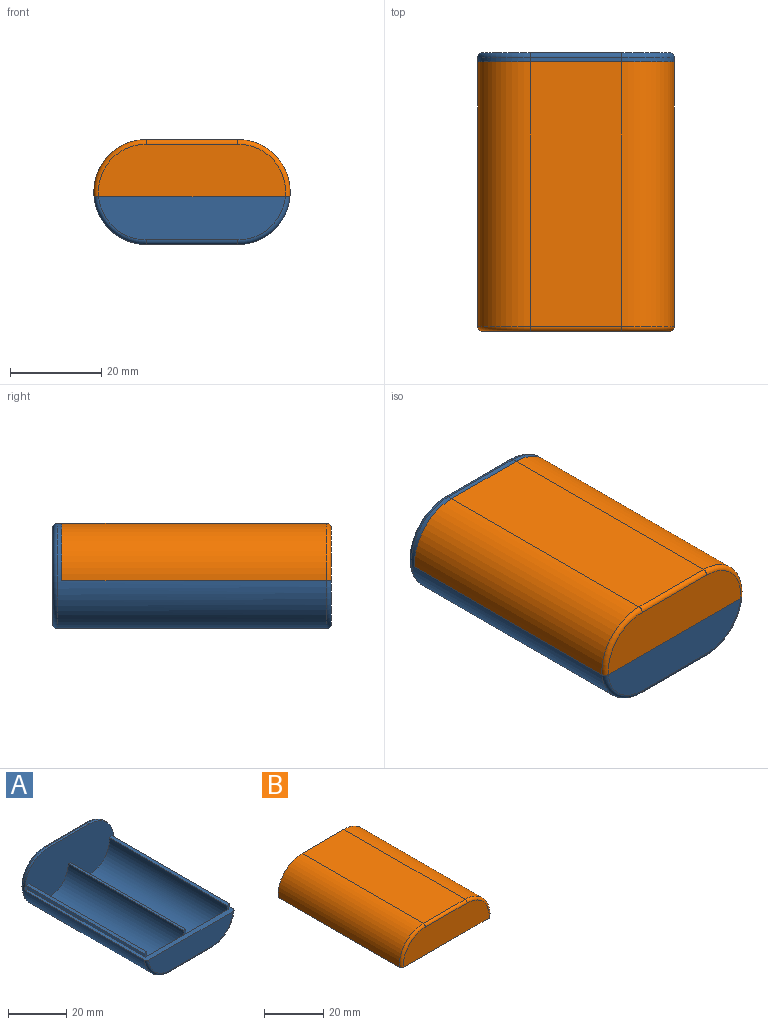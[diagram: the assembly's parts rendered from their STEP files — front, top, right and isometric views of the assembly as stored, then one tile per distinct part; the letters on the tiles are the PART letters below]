
ASSEMBLY  parts=2 mates=1
PART A: 27 faces, bbox 44.9x61x24.9 mm
  f0: plane 2x1.42mm, normal (0,-1,0), area 2mm2, adj f10,f11,f12,f13
  f1: plane 2x1.42mm, normal (0,-1,0), area 2mm2, adj f7,f8,f9,f10
  f2: cylinder r=11.5mm len=59mm, axis (0,-1,0), area 1025.8mm2, adj f3,f5,f10,f15,f20,f25
  f3: plane 20x1mm, normal (0,0,1), area 20mm2, adj f2,f4,f15,f21
  f4: cylinder r=11.5mm len=59mm, axis (0,-1,0), area 1025.8mm2, adj f3,f5,f10,f15,f23,f24
  f5: plane 59x20mm, normal (0,0,-1), area 1180mm2, adj f2,f4,f22,f26
  f6: plane 41x21mm, normal (0,1,0), area 766.4mm2, adj f20,f21,f22,f23
  f7: cylinder r=9.5mm len=57mm, axis (0,-1,0), area 1743.4mm2, adj f1,f8,f14,f15,f16,f18,f19
  f8: plane 57x1.42mm, normal (0,0,1), area 80.8mm2, adj f1,f7,f9,f15
  f9: plane 57x2mm, normal (0.94,0,-0.34), area 121.3mm2, adj f1,f8,f10,f15
  f10: plane 59x42.91mm, normal (0,0,1), area 235.9mm2, adj f0,f1,f2,f4,f9,f11,f15,f16
  f11: plane 57x2mm, normal (-0.94,0,-0.34), area 121.3mm2, adj f0,f10,f12,f15
  f12: plane 57x1.42mm, normal (0,0,1), area 80.8mm2, adj f0,f11,f13,f15
  f13: cylinder r=9.5mm len=57mm, axis (0,-1,0), area 1743.4mm2, adj f0,f12,f14,f15,f16,f18,f19
  f14: plane 56x1mm, normal (0,0,1), area 56mm2, adj f7,f13,f15,f19
  f15: plane 43x21mm, normal (0,-1,0), area 721.2mm2, adj f2,f3,f4,f7,f8,f9,f10,f11
  f16: plane 38.89x8.5mm, normal (0,1,0), area 292.8mm2, adj f7,f10,f13,f18
  f17: plane 40.9x9.5mm, normal (0,-1,0), area 342.2mm2, adj f10,f24,f25,f26
  f18: plane 20x1mm, normal (0,0,1), area 20mm2, adj f7,f13,f16,f19
  f19: plane 20x9.5mm, normal (0,-1,0), area 48.2mm2, adj f7,f13,f14,f18
  f20: torus R=10.5mm, axis (0,-1,0), area 55mm2, adj f2,f6,f21,f22
  f21: cylinder r=1mm len=20mm, axis (1,0,0), area 31.4mm2, adj f3,f6,f20,f23
  f22: cylinder r=1mm len=20mm, axis (-1,0,0), area 31.4mm2, adj f5,f6,f20,f23
  f23: torus R=10.5mm, axis (0,-1,0), area 55mm2, adj f4,f6,f21,f22
  f24: torus R=10.5mm, axis (0,-1,0), area 25.9mm2, adj f4,f10,f17,f26
  f25: torus R=10.5mm, axis (0,-1,0), area 25.9mm2, adj f2,f10,f17,f26
  f26: cylinder r=1mm len=20mm, axis (1,0,0), area 31.4mm2, adj f5,f17,f24,f25
PART B: 17 faces, bbox 44.9x59x13.6 mm
  f0: cylinder r=9.5mm len=57mm, axis (0,-1,0), area 793.5mm2, adj f1,f10,f11,f12
  f1: plane 57x1.42mm, normal (0,0,-1), area 80.8mm2, adj f0,f2,f11,f12
  f2: plane 57x2mm, normal (-0.94,0,0.34), area 121.3mm2, adj f1,f6,f11,f12
  f3: cylinder r=11.5mm len=58mm, axis (0,-1,0), area 1105.8mm2, adj f4,f6,f11,f16
  f4: plane 58x20mm, normal (0,0,1), area 1160mm2, adj f3,f5,f11,f15
  f5: cylinder r=11.5mm len=58mm, axis (0,-1,0), area 1105.8mm2, adj f4,f6,f11,f14
  f6: plane 59x42.91mm, normal (0,0,-1), area 235.9mm2, adj f2,f3,f5,f7,f11,f12,f13,f14
  f7: plane 57x2mm, normal (0.94,0,0.34), area 121.3mm2, adj f6,f8,f11,f12
  f8: plane 57x1.42mm, normal (0,0,-1), area 80.8mm2, adj f7,f9,f11,f12
  f9: cylinder r=9.5mm len=57mm, axis (0,-1,0), area 793.5mm2, adj f8,f10,f11,f12
  f10: plane 57x20mm, normal (0,0,-1), area 1140mm2, adj f0,f9,f11,f12
  f11: plane 43x12.5mm, normal (0,1,0), area 105.9mm2, adj f0,f1,f2,f3,f4,f5,f6,f7
  f12: plane 41.73x10.5mm, normal (0,1,0), area 374.8mm2, adj f0,f1,f2,f6,f7,f8,f9,f10
  f13: plane 41x11.5mm, normal (0,-1,0), area 424.1mm2, adj f6,f14,f15,f16
  f14: torus R=10.5mm, axis (0,-1,0), area 29.1mm2, adj f5,f6,f13,f15
  f15: cylinder r=1mm len=20mm, axis (-1,0,0), area 31.4mm2, adj f4,f13,f14,f16
  f16: torus R=10.5mm, axis (0,-1,0), area 29.1mm2, adj f3,f6,f13,f15
PLACE A t=(-39.09,-111.98,-40.73)mm
PLACE B t=(-39.09,-111.98,-40.73)mm
MATE fastened B.f6 <-> A.f10  axis (0,0,-1) through (-17.59,-94.15,-30.23)mm
